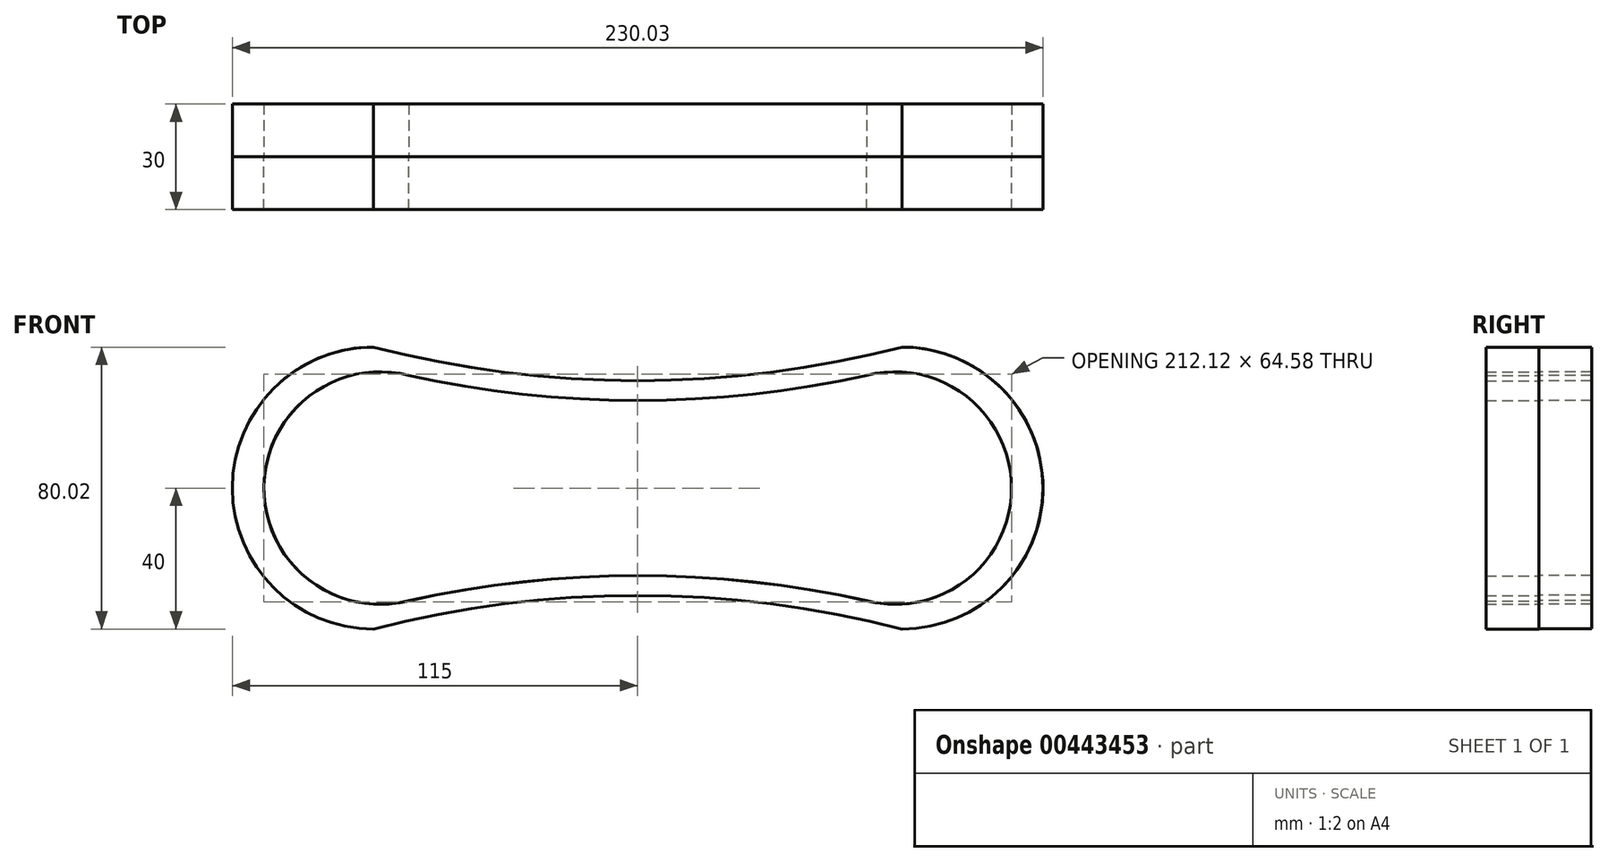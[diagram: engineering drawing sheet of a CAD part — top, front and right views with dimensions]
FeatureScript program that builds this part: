
annotation { "Feature Type Name" : "Feature", "Feature Type Description" : "" }
export const myFeature = defineFeature(function(context is Context, id is Id, definition is map)
    precondition{}
    {
        {
            var Q0;
            Q0=qCreatedBy(makeId("Front.planeOp"),FACE);
            var sketch = newSketch(context, id + "F0", { "sketchPlane" : qUnion([Q0])});
            skArc(sketch, "E0", {"start": v(75, -40) * mm, "mid": v(115, 0) * mm, "end": v(75, 40) * mm});
            skArc(sketch, "E1", {"start": v(-75, 40) * mm, "mid": v(-115, 0) * mm, "end": v(-75, -40) * mm});
            skArc(sketch, "E2", {"start": v(-75, 40) * mm, "mid": v(0, 30.47) * mm, "end": v(75, 40) * mm});
            skArc(sketch, "E3", {"start": v(75, -40) * mm, "mid": v(0, -30.47) * mm, "end": v(-75, -40) * mm});
            skPoint(sketch, "E4.middle", {"position": v(0, 0) * mm});
            skArc(sketch, "E5", {"start": v(-65, 32) * mm, "mid": v(0, 24.87) * mm, "end": v(65, 32) * mm});
            skArc(sketch, "E6", {"start": v(65, -32) * mm, "mid": v(0, -24.87) * mm, "end": v(-65, -32) * mm});
            skArc(sketch, "E7", {"start": v(-65, 32) * mm, "mid": v(-106.06, 0) * mm, "end": v(-65, -32) * mm});
            skArc(sketch, "E8", {"start": v(65, -32) * mm, "mid": v(106.06, 0) * mm, "end": v(65, 32) * mm});
            skSolve(sketch);
        }
        {
            var Q0;
            Q0=makeQuery(id+"F0.imprint","IMPRINT",FACE,{"disambiguationData":[TD([[makeQuery(id+"F0.imprint","IMPRINT",EDGE,{"derivedFrom":sQuery(id+"F0.wireOp",EDGE,"E0")}),1.0]])]});
            extrude(context, id + "F1", {"entities" : qUnion([Q0]), "depth" : 15 * mm});
        }
        {
            var Q0;
            Q0=qCreatedBy(makeId("Front.planeOp"),FACE);
            var sketch = newSketch(context, id + "F2", { "sketchPlane" : qUnion([Q0])});
            skArc(sketch, "E9", {"start": v(75.03, -39.98) * mm, "mid": v(115.03, 0.02) * mm, "end": v(75.03, 40.02) * mm});
            skArc(sketch, "E10", {"start": v(-74.97, 40.02) * mm, "mid": v(-114.97, 0.02) * mm, "end": v(-74.97, -39.98) * mm});
            skArc(sketch, "E11", {"start": v(-74.97, 40.02) * mm, "mid": v(0.03, 30.5) * mm, "end": v(75.03, 40.02) * mm});
            skArc(sketch, "E12", {"start": v(75.03, -39.98) * mm, "mid": v(0.03, -30.45) * mm, "end": v(-74.97, -39.98) * mm});
            skPoint(sketch, "E13.middle", {"position": v(0.03, 0.02) * mm});
            skArc(sketch, "E14", {"start": v(-64.97, 32.02) * mm, "mid": v(0.03, 24.9) * mm, "end": v(65.03, 32.02) * mm});
            skArc(sketch, "E15", {"start": v(65.03, -31.98) * mm, "mid": v(0.03, -24.85) * mm, "end": v(-64.97, -31.98) * mm});
            skArc(sketch, "E16", {"start": v(-64.97, 32.02) * mm, "mid": v(-106.04, 0.02) * mm, "end": v(-64.97, -31.98) * mm});
            skArc(sketch, "E17", {"start": v(65.03, -31.98) * mm, "mid": v(106.09, 0.02) * mm, "end": v(65.03, 32.02) * mm});
            skSolve(sketch);
        }
        {
            var Q0;
            Q0=qSketchRegion(id+"F2",true);
            extrude(context, id + "F3", {"entities" : qUnion([Q0]), "operationType" : NewBodyOperationType.ADD, "oppositeDirection" : true, "depth" : 15 * mm});
        }
    });
